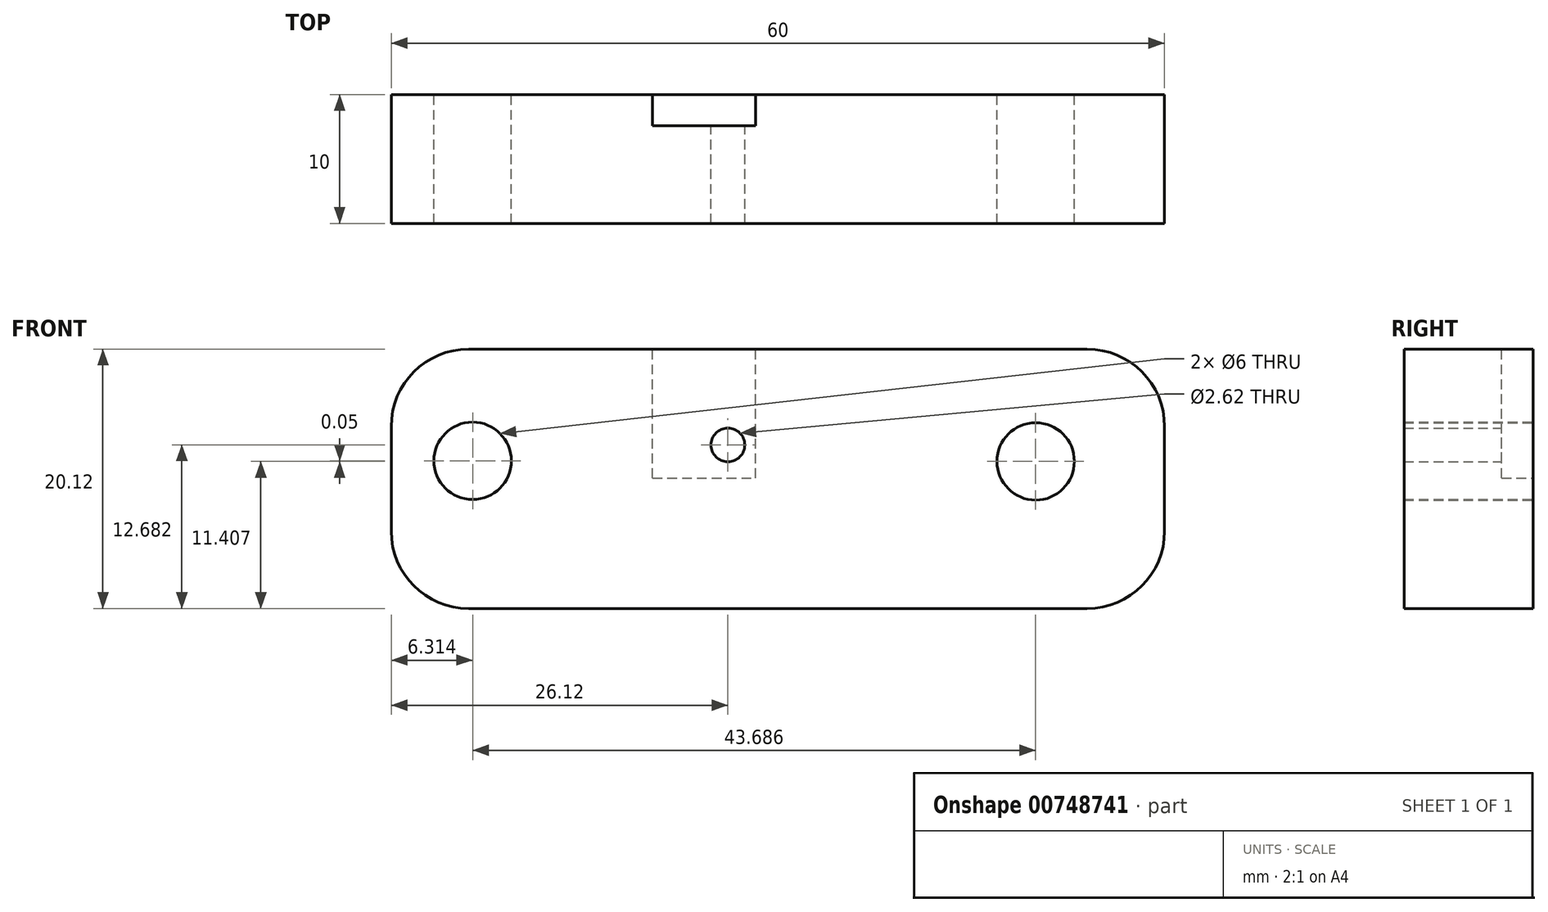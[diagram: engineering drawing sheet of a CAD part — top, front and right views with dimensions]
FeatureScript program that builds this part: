
annotation { "Feature Type Name" : "Feature", "Feature Type Description" : "" }
export const myFeature = defineFeature(function(context is Context, id is Id, definition is map)
    precondition{}
    {
        {
            var Q0;
            Q0=qCreatedBy(makeId("Front.planeOp"),FACE);
            var sketch = newSketch(context, id + "F0", { "sketchPlane" : qUnion([Q0])});
            skLineSegment(sketch, "E0.bottom", {"start": v(0, 0) * mm, "end": v(60, 0) * mm});
            skLineSegment(sketch, "E0.top", {"start": v(0, 20.12) * mm, "end": v(60, 20.12) * mm});
            skLineSegment(sketch, "E0.left", {"start": v(0, 0) * mm, "end": v(0, 20.12) * mm});
            skLineSegment(sketch, "E0.right", {"start": v(60, 0) * mm, "end": v(60, 20.12) * mm});
            skCircle(sketch, "E1", {"center": v(6.31, 11.46) * mm, "radius": 3 * mm});
            skCircle(sketch, "E2", {"center": v(50, 11.4) * mm, "radius": 3 * mm});
            skCircle(sketch, "E3", {"center": v(26.12, 12.68) * mm, "radius": 1.3 * mm});
            skSolve(sketch);
        }
        {
            var Q0;
            Q0=makeQuery(id+"F0.imprint","IMPRINT",FACE,{"disambiguationData":[TD([[makeQuery(id+"F0.imprint","IMPRINT",EDGE,{"derivedFrom":sQuery(id+"F0.wireOp",EDGE,"E0.bottom")}),1.0]])]});
            extrude(context, id + "F1", {"entities" : qUnion([Q0]), "depth" : 10 * mm});
        }
        {
            var Q0;
            Q0=makeQuery(id+"F1.opExtrude","CAP_FACE",FACE,{"disambiguationData":[OSD([sQuery(id+"F0.wireOp",EDGE,"E0.bottom"),sQuery(id+"F0.wireOp",EDGE,"E0.top"),sQuery(id+"F0.wireOp",EDGE,"E0.left"),sQuery(id+"F0.wireOp",EDGE,"E0.right"),sQuery(id+"F0.wireOp",EDGE,"E1"),sQuery(id+"F0.wireOp",EDGE,"E2"),sQuery(id+"F0.wireOp",EDGE,"E3")])],"isStart":true});
            var sketch = newSketch(context, id + "F2", { "sketchPlane" : qUnion([Q0])});
            skLineSegment(sketch, "E4.bottom", {"start": v(-18.36, 10) * mm, "end": v(-20.17, 10) * mm});
            skLineSegment(sketch, "E4.top", {"start": v(-18.36, 7.06) * mm, "end": v(-20.17, 7.06) * mm});
            skLineSegment(sketch, "E4.left", {"start": v(-18.36, 10) * mm, "end": v(-18.36, 7.06) * mm});
            skLineSegment(sketch, "E4.right", {"start": v(-20.17, 10) * mm, "end": v(-20.17, 7.06) * mm});
            skSolve(sketch);
        }
        {
            var Q0;
            Q0=makeQuery(id+"F1.opExtrude","SWEPT_EDGE",EDGE,{"disambiguationData":[OSD([sQuery(id+"F0.wireOp",EDGE,"E0.bottom"),sQuery(id+"F0.wireOp",EDGE,"E0.left")])]});
            var Q1;
            Q1=makeQuery(id+"F1.opExtrude","SWEPT_EDGE",EDGE,{"disambiguationData":[OSD([sQuery(id+"F0.wireOp",EDGE,"E0.top"),sQuery(id+"F0.wireOp",EDGE,"E0.left")])]});
            var Q2;
            Q2=makeQuery(id+"F1.opExtrude","SWEPT_EDGE",EDGE,{"disambiguationData":[OSD([sQuery(id+"F0.wireOp",EDGE,"E0.bottom"),sQuery(id+"F0.wireOp",EDGE,"E0.right")])]});
            var Q3;
            Q3=makeQuery(id+"F1.opExtrude","SWEPT_EDGE",EDGE,{"disambiguationData":[OSD([sQuery(id+"F0.wireOp",EDGE,"E0.top"),sQuery(id+"F0.wireOp",EDGE,"E0.right")])]});
            fillet(context, id + "F3", {"entities" : qUnion([Q0, Q1, Q2, Q3]), "radius" : 6 * mm, "tangentPropagation" : true, "allowEdgeOverflow" : false});
        }
        {
            var Q0;
            Q0=makeQuery(id+"F1.opExtrude","SWEPT_FACE",FACE,{"disambiguationData":[OSD([sQuery(id+"F0.wireOp",EDGE,"E0.top")])]});
            var sketch = newSketch(context, id + "F4", { "sketchPlane" : qUnion([Q0])});
            skLineSegment(sketch, "E5.bottom", {"start": v(20.28, -2.43) * mm, "end": v(28.27, -2.43) * mm});
            skLineSegment(sketch, "E5.top", {"start": v(20.28, 0) * mm, "end": v(28.27, 0) * mm});
            skLineSegment(sketch, "E5.left", {"start": v(20.28, -2.43) * mm, "end": v(20.28, 0) * mm});
            skLineSegment(sketch, "E5.right", {"start": v(28.27, -2.43) * mm, "end": v(28.27, 0) * mm});
            skSolve(sketch);
        }
        {
            var Q0;
            Q0=makeQuery(id+"F4.imprint","IMPRINT",FACE,{"disambiguationData":[TD([[makeQuery(id+"F4.imprint","IMPRINT",EDGE,{"derivedFrom":sQuery(id+"F4.wireOp",EDGE,"E5.bottom")}),1.0]])]});
            extrude(context, id + "F5", {"entities" : qUnion([Q0]), "operationType" : NewBodyOperationType.REMOVE, "oppositeDirection" : true, "depth" : 10 * mm});
        }
    });
